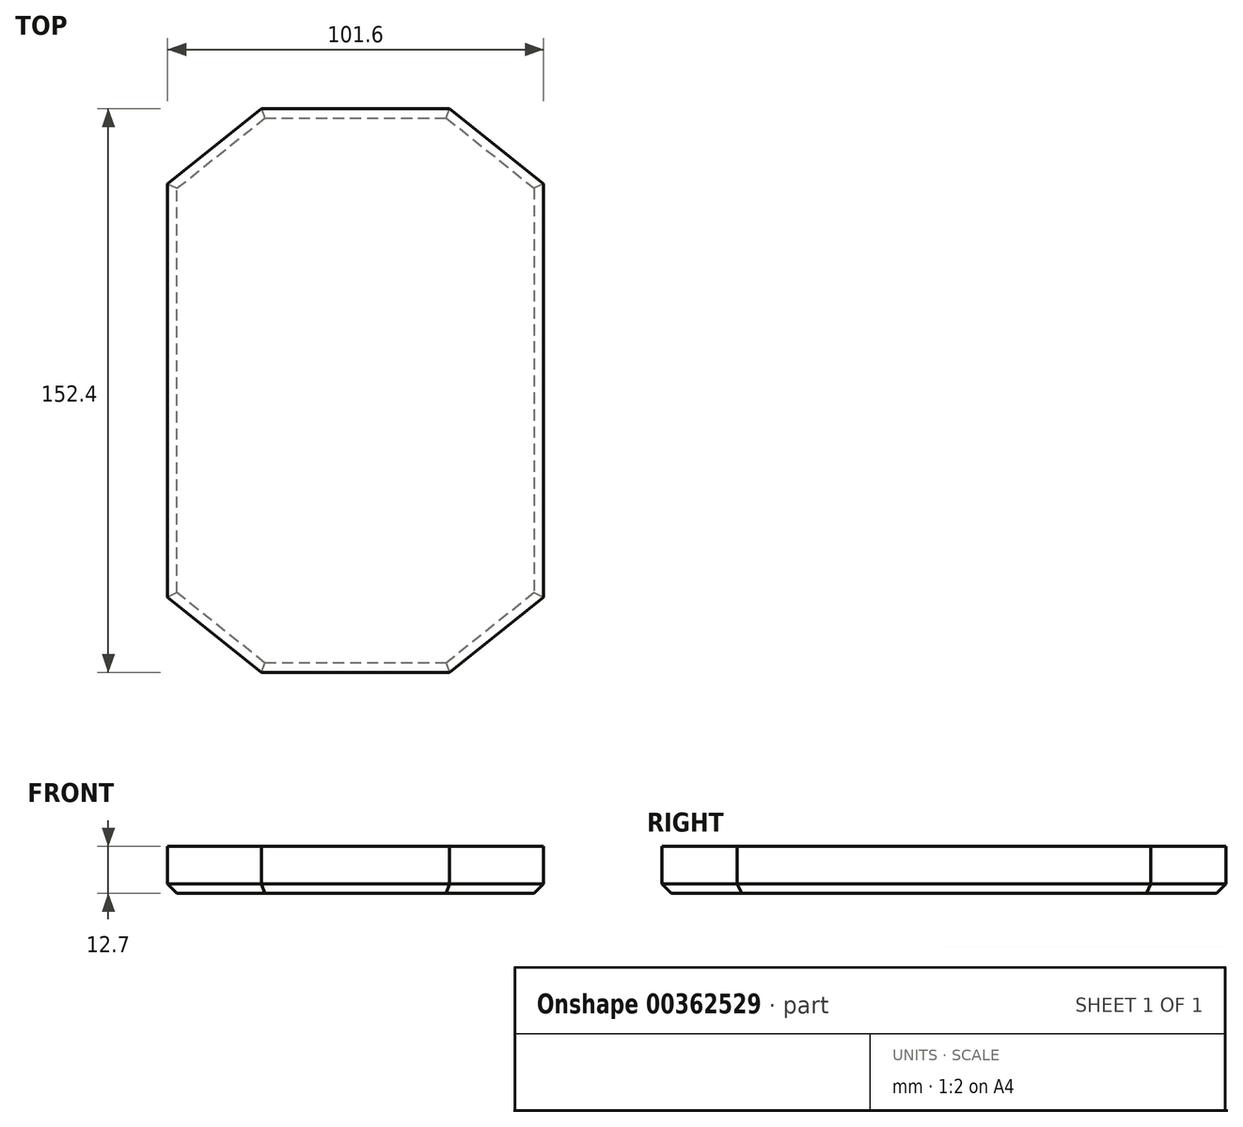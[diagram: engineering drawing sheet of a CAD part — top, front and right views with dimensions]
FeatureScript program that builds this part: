
annotation { "Feature Type Name" : "Feature", "Feature Type Description" : "" }
export const myFeature = defineFeature(function(context is Context, id is Id, definition is map)
    precondition{}
    {
        {
            var Q0;
            Q0=qCreatedBy(makeId("Top.planeOp"),FACE);
            var sketch = newSketch(context, id + "F0", { "sketchPlane" : qUnion([Q0])});
            skLineSegment(sketch, "E0", {"start": v(0, 0) * mm, "end": v(0, 76.2) * mm});
            skLineSegment(sketch, "E1", {"start": v(0, 76.2) * mm, "end": v(25.4, 76.2) * mm});
            skLineSegment(sketch, "E2", {"start": v(0, 76.2) * mm, "end": v(-25.4, 76.2) * mm});
            skLineSegment(sketch, "E3", {"start": v(0, 0) * mm, "end": v(50.8, 0) * mm});
            skLineSegment(sketch, "E4", {"start": v(0, 0) * mm, "end": v(-50.8, 0) * mm});
            skLineSegment(sketch, "E5", {"start": v(-50.8, 0) * mm, "end": v(-50.8, 55.88) * mm});
            skLineSegment(sketch, "E6", {"start": v(50.8, 0) * mm, "end": v(50.8, 55.88) * mm});
            skLineSegment(sketch, "E7", {"start": v(-25.4, 76.2) * mm, "end": v(-50.8, 55.88) * mm});
            skLineSegment(sketch, "E8", {"start": v(25.4, 76.2) * mm, "end": v(50.8, 55.88) * mm});
            skLineSegment(sketch, "E9.MirrorCS", {"start": v(0, -76.2) * mm, "end": v(-25.4, -76.2) * mm});
            skLineSegment(sketch, "E10.MirrorCS", {"start": v(0, 0) * mm, "end": v(0, -76.2) * mm});
            skLineSegment(sketch, "E11.MirrorCS", {"start": v(0, -76.2) * mm, "end": v(25.4, -76.2) * mm});
            skLineSegment(sketch, "E12.MirrorCS", {"start": v(50.8, 0) * mm, "end": v(50.8, -55.88) * mm});
            skLineSegment(sketch, "E13.MirrorCS", {"start": v(-25.4, -76.2) * mm, "end": v(-50.8, -55.88) * mm});
            skLineSegment(sketch, "E14.MirrorCS", {"start": v(-50.8, 0) * mm, "end": v(-50.8, -55.88) * mm});
            skLineSegment(sketch, "E15.MirrorCS", {"start": v(25.4, -76.2) * mm, "end": v(50.8, -55.88) * mm});
            skSolve(sketch);
        }
        {
            var Q0;
            Q0=makeQuery(id+"F0.imprint","IMPRINT",FACE,{"disambiguationData":[TD([[makeQuery(id+"F0.imprint","IMPRINT",EDGE,{"derivedFrom":sQuery(id+"F0.wireOp",EDGE,"E0")}),-1.0]])]});
            var Q1;
            Q1=makeQuery(id+"F0.imprint","IMPRINT",FACE,{"disambiguationData":[TD([[makeQuery(id+"F0.imprint","IMPRINT",EDGE,{"derivedFrom":sQuery(id+"F0.wireOp",EDGE,"E0")}),1.0]])]});
            var Q2;
            Q2=makeQuery(id+"F0.imprint","IMPRINT",FACE,{"disambiguationData":[TD([[makeQuery(id+"F0.imprint","IMPRINT",EDGE,{"derivedFrom":sQuery(id+"F0.wireOp",EDGE,"E4")}),1.0]])]});
            var Q3;
            Q3=makeQuery(id+"F0.imprint","IMPRINT",FACE,{"disambiguationData":[TD([[makeQuery(id+"F0.imprint","IMPRINT",EDGE,{"derivedFrom":sQuery(id+"F0.wireOp",EDGE,"E3")}),-1.0]])]});
            extrude(context, id + "F1", {"entities" : qUnion([Q0, Q1, Q2, Q3]), "depth" : 12.7 * mm});
        }
        {
            var Q0;
            Q0=makeQuery(id+"F1.opExtrude","CAP_FACE",FACE,{"disambiguationData":[OSD([sQuery(id+"F0.wireOp",EDGE,"E1"),sQuery(id+"F0.wireOp",EDGE,"E2"),sQuery(id+"F0.wireOp",EDGE,"E5"),sQuery(id+"F0.wireOp",EDGE,"E6"),sQuery(id+"F0.wireOp",EDGE,"E7"),sQuery(id+"F0.wireOp",EDGE,"E8"),sQuery(id+"F0.wireOp",EDGE,"E9.MirrorCS"),sQuery(id+"F0.wireOp",EDGE,"E11.MirrorCS"),sQuery(id+"F0.wireOp",EDGE,"E12.MirrorCS"),sQuery(id+"F0.wireOp",EDGE,"E13.MirrorCS"),sQuery(id+"F0.wireOp",EDGE,"E14.MirrorCS"),sQuery(id+"F0.wireOp",EDGE,"E15.MirrorCS")])],"isStart":true});
            chamfer(context, id + "F2", {"entities" : qUnion([Q0]), "width" : 2.54 * mm, "tangentPropagation" : true});
        }
    });
